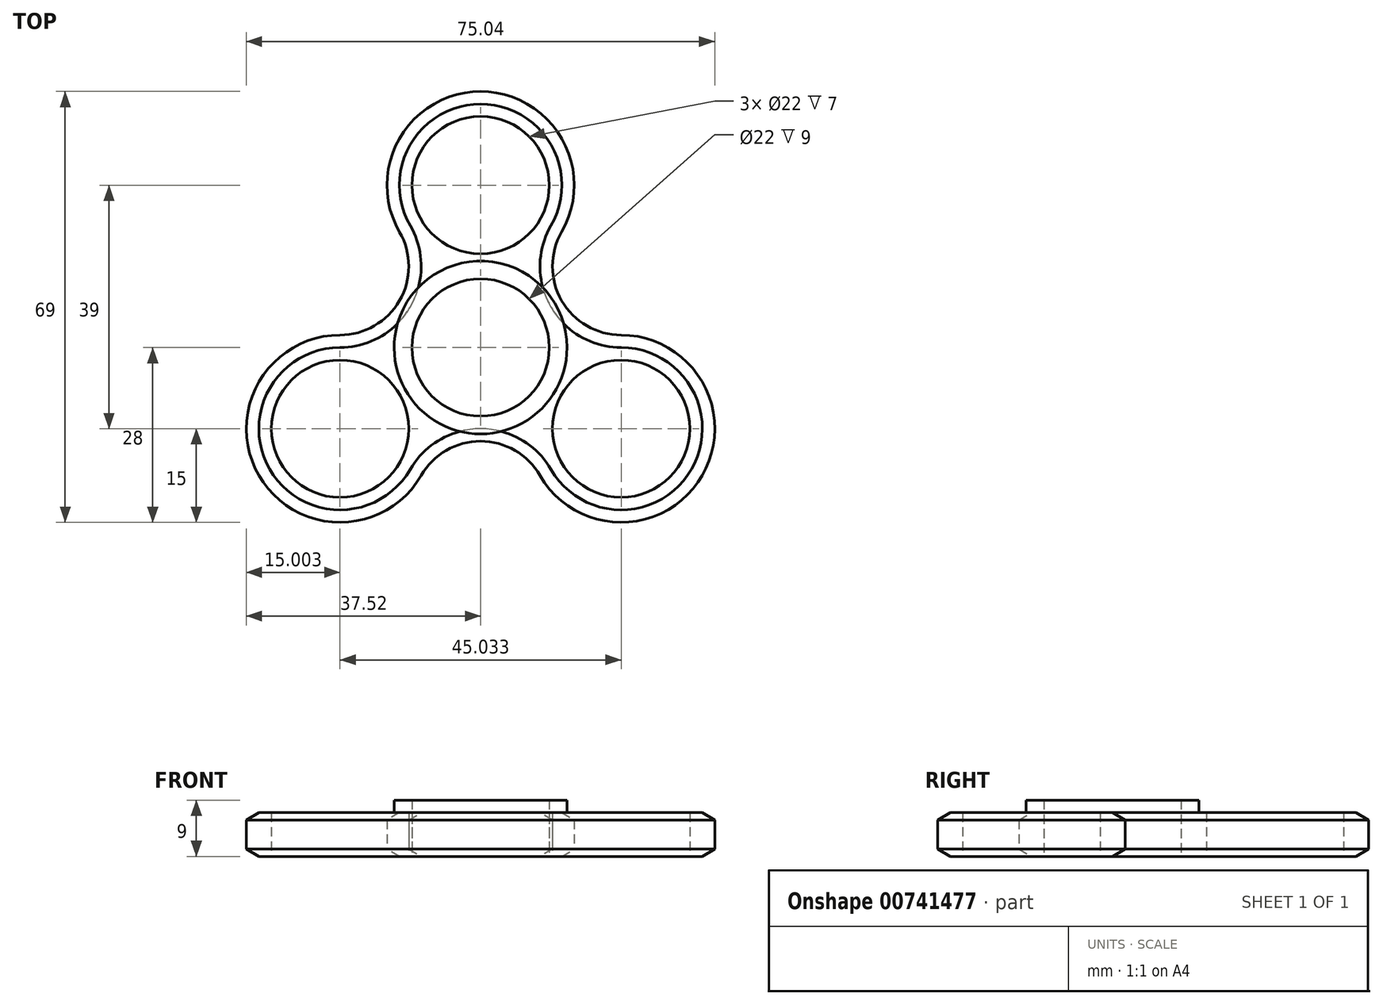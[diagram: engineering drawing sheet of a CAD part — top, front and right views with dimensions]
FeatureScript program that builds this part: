
annotation { "Feature Type Name" : "Feature", "Feature Type Description" : "" }
export const myFeature = defineFeature(function(context is Context, id is Id, definition is map)
    precondition{}
    {
        {
            var Q0;
            Q0=qCreatedBy(makeId("Top.planeOp"),FACE);
            var sketch = newSketch(context, id + "F0", { "sketchPlane" : qUnion([Q0])});
            skCircle(sketch, "E0", {"center": v(0, 26) * mm, "radius": 11 * mm});
            skCircle(sketch, "E1", {"center": v(-22.52, -13) * mm, "radius": 11 * mm});
            skCircle(sketch, "E2", {"center": v(22.52, -13) * mm, "radius": 11 * mm});
            skCircle(sketch, "E3", {"center": v(0, 0) * mm, "radius": 11 * mm});
            skCircle(sketch, "E4", {"center": v(0, 0) * mm, "radius": 26 * mm, "construction": true});
            skLineSegment(sketch, "E5", {"start": v(0, 26) * mm, "end": v(0, 0) * mm, "construction": true});
            skLineSegment(sketch, "E6", {"start": v(0, 0) * mm, "end": v(22.52, -13) * mm, "construction": true});
            skLineSegment(sketch, "E7", {"start": v(0, 0) * mm, "end": v(-22.52, -13) * mm, "construction": true});
            skCircle(sketch, "E8", {"center": v(0, 0) * mm, "radius": 37 * mm, "construction": true});
            skArc(sketch, "E9", {"start": v(-9.53, -20.5) * mm, "mid": v(-35.5, -20.5) * mm, "end": v(-22.52, 2) * mm});
            skArc(sketch, "E10", {"start": v(9.53, -20.5) * mm, "mid": v(35.5, -20.5) * mm, "end": v(22.52, 2) * mm});
            skArc(sketch, "E11", {"start": v(-13, 18.5) * mm, "mid": v(0, 41) * mm, "end": v(13, 18.5) * mm});
            skLineSegment(sketch, "E12", {"start": v(0, 0) * mm, "end": v(0, -26) * mm, "construction": true});
            skLineSegment(sketch, "E13", {"start": v(0, 0) * mm, "end": v(-22.52, 13) * mm, "construction": true});
            skLineSegment(sketch, "E14", {"start": v(0, 0) * mm, "end": v(22.52, 13) * mm, "construction": true});
            skLineSegment(sketch, "E15", {"start": v(-9.53, -20.5) * mm, "end": v(-9.53, -20.5) * mm});
            skLineSegment(sketch, "E16", {"start": v(-13, 18.5) * mm, "end": v(-13, 18.5) * mm});
            skLineSegment(sketch, "E17", {"start": v(13, 18.5) * mm, "end": v(13, 18.5) * mm});
            skLineSegment(sketch, "E18", {"start": v(22.52, 2) * mm, "end": v(22.52, 2) * mm});
            skLineSegment(sketch, "E19", {"start": v(9.53, -20.5) * mm, "end": v(9.53, -20.5) * mm});
            skArc(sketch, "E20", {"start": v(-13, 18.5) * mm, "mid": v(-13, 7.5) * mm, "end": v(-22.52, 2) * mm});
            skArc(sketch, "E21", {"start": v(13, 18.5) * mm, "mid": v(13, 7.5) * mm, "end": v(22.52, 2) * mm});
            skArc(sketch, "E22", {"start": v(9.53, -20.5) * mm, "mid": v(0, -15) * mm, "end": v(-9.53, -20.5) * mm});
            skCircle(sketch, "E23", {"center": v(0, 0) * mm, "radius": 15 * mm, "construction": true});
            skCircle(sketch, "E24", {"center": v(0, 0) * mm, "radius": 41 * mm, "construction": true});
            skLineSegment(sketch, "E25", {"start": v(-22.52, 2) * mm, "end": v(-22.52, 2) * mm});
            skSolve(sketch);
        }
        {
            var Q0;
            Q0 = qSketchRegion(id + "F0", true);
            extrude(context, id + "F1", {"entities" : qUnion([Q0]), "endBound" : BoundingType.SYMMETRIC, "depth" : 7 * mm, "offsetDistance" : 25 * mm});
        }
        {
            var Q0;
            Q0=qCreatedBy(makeId("Top.planeOp"),FACE);
            var sketch = newSketch(context, id + "F2", { "sketchPlane" : qUnion([Q0])});
            skCircle(sketch, "E26", {"center": v(0, 0) * mm, "radius": 11 * mm});
            skSolve(sketch);
        }
        {
            var Q0;
            Q0 = qSketchRegion(id + "F2", true);
            extrude(context, id + "F3", {"entities" : qUnion([Q0]), "operationType" : NewBodyOperationType.REMOVE, "endBound" : BoundingType.THROUGH_ALL, "oppositeDirection" : true, "depth" : 25 * mm, "offsetDistance" : 25 * mm, "hasSecondDirection" : true, "secondDirectionBound" : SecondDirectionBoundingType.THROUGH_ALL, "secondDirectionOppositeDirection" : false, "secondDirectionDepth" : 25 * mm});
        }
        {
            var Q0;
            Q0=makeQuery(id+"F1.opExtrude","CAP_EDGE",EDGE,{"disambiguationData":[OSD([sQuery(id+"F0.wireOp",EDGE,"E9")])],"isStart":false});
            var Q1;
            Q1=makeQuery(id+"F1.opExtrude","CAP_EDGE",EDGE,{"disambiguationData":[OSD([sQuery(id+"F0.wireOp",EDGE,"E9")])],"isStart":true});
            var Q2;
            Q2=makeQuery(id+"F3.boolean.opBoolean","INTERSECT",EDGE,{"derivedFrom":[makeQuery(id+"F1.opExtrude","CAP_FACE",FACE,{"disambiguationData":[OSD([sQuery(id+"F0.wireOp",EDGE,"E0"),sQuery(id+"F0.wireOp",EDGE,"E1"),sQuery(id+"F0.wireOp",EDGE,"E2"),sQuery(id+"F0.wireOp",EDGE,"XNPakRHv-zOhi-0FM5-hTdu-OG3i7tiAVQxY"),sQuery(id+"F0.wireOp",EDGE,"E9"),sQuery(id+"F0.wireOp",EDGE,"dCo0jm6D-gOeC-fFHZ-glrm-1aHonwMQvqJC"),sQuery(id+"F0.wireOp",EDGE,"E10"),sQuery(id+"F0.wireOp",EDGE,"E11"),sQuery(id+"F0.wireOp",EDGE,"YkruY3tB-21v4-OKZR-qZbx-QCQuqMLywjzG"),sQuery(id+"F0.wireOp",EDGE,"SekSoQT0-foV7-ICcH-uNWv-8Mtw90ad5pJT"),sQuery(id+"F0.wireOp",EDGE,"o91gRGPa-Ibxz-ax7s-b3tE-83rfG7TcEAhW"),sQuery(id+"F0.wireOp",EDGE,"bdXiWe1d-0TL7-GA1S-cq4B-UudjERh8iepl")])],"isStart":true}),makeQuery(id+"F3.opExtrude","SWEPT_FACE",FACE,{"disambiguationData":[OSD([sQuery(id+"F2.wireOp",EDGE,"E26")])]})]});
            var Q3;
            Q3=makeQuery(id+"F3.boolean.opBoolean","INTERSECT",EDGE,{"derivedFrom":[makeQuery(id+"F1.opExtrude","CAP_FACE",FACE,{"disambiguationData":[OSD([sQuery(id+"F0.wireOp",EDGE,"E0"),sQuery(id+"F0.wireOp",EDGE,"E1"),sQuery(id+"F0.wireOp",EDGE,"E2"),sQuery(id+"F0.wireOp",EDGE,"XNPakRHv-zOhi-0FM5-hTdu-OG3i7tiAVQxY"),sQuery(id+"F0.wireOp",EDGE,"E9"),sQuery(id+"F0.wireOp",EDGE,"dCo0jm6D-gOeC-fFHZ-glrm-1aHonwMQvqJC"),sQuery(id+"F0.wireOp",EDGE,"E10"),sQuery(id+"F0.wireOp",EDGE,"E11"),sQuery(id+"F0.wireOp",EDGE,"YkruY3tB-21v4-OKZR-qZbx-QCQuqMLywjzG"),sQuery(id+"F0.wireOp",EDGE,"SekSoQT0-foV7-ICcH-uNWv-8Mtw90ad5pJT"),sQuery(id+"F0.wireOp",EDGE,"o91gRGPa-Ibxz-ax7s-b3tE-83rfG7TcEAhW"),sQuery(id+"F0.wireOp",EDGE,"bdXiWe1d-0TL7-GA1S-cq4B-UudjERh8iepl")])],"isStart":false}),makeQuery(id+"F3.opExtrude","SWEPT_FACE",FACE,{"disambiguationData":[OSD([sQuery(id+"F2.wireOp",EDGE,"E26")])]})]});
            chamfer(context, id + "F4", {"entities" : qUnion([Q0, Q1, Q2, Q3]), "chamferType" : ChamferType.OFFSET_ANGLE, "width" : 2 * mm, "oppositeDirection" : false, "angle" : 30 * degree, "tangentPropagation" : true});
        }
        {
            var Q0;
            Q0=makeQuery(id+"F1.opExtrude","CAP_FACE",FACE,{"disambiguationData":[OSD([sQuery(id+"F0.wireOp",EDGE,"E0"),sQuery(id+"F0.wireOp",EDGE,"E1"),sQuery(id+"F0.wireOp",EDGE,"E2"),sQuery(id+"F0.wireOp",EDGE,"E3"),sQuery(id+"F0.wireOp",EDGE,"E9"),sQuery(id+"F0.wireOp",EDGE,"E10"),sQuery(id+"F0.wireOp",EDGE,"E11"),sQuery(id+"F0.wireOp",EDGE,"E20"),sQuery(id+"F0.wireOp",EDGE,"E21"),sQuery(id+"F0.wireOp",EDGE,"E22")])],"isStart":false});
            var sketch = newSketch(context, id + "F5", { "sketchPlane" : qUnion([Q0])});
            skCircle(sketch, "E27", {"center": v(0, 0) * mm, "radius": 11 * mm});
            skCircle(sketch, "E28", {"center": v(0, 0) * mm, "radius": 13.85 * mm});
            skSolve(sketch);
        }
        {
            var Q0;
            Q0 = qSketchRegion(id + "F5", true);
            extrude(context, id + "F6", {"entities" : qUnion([Q0]), "operationType" : NewBodyOperationType.ADD, "depth" : 2 * mm, "offsetDistance" : 25 * mm});
        }
    });
